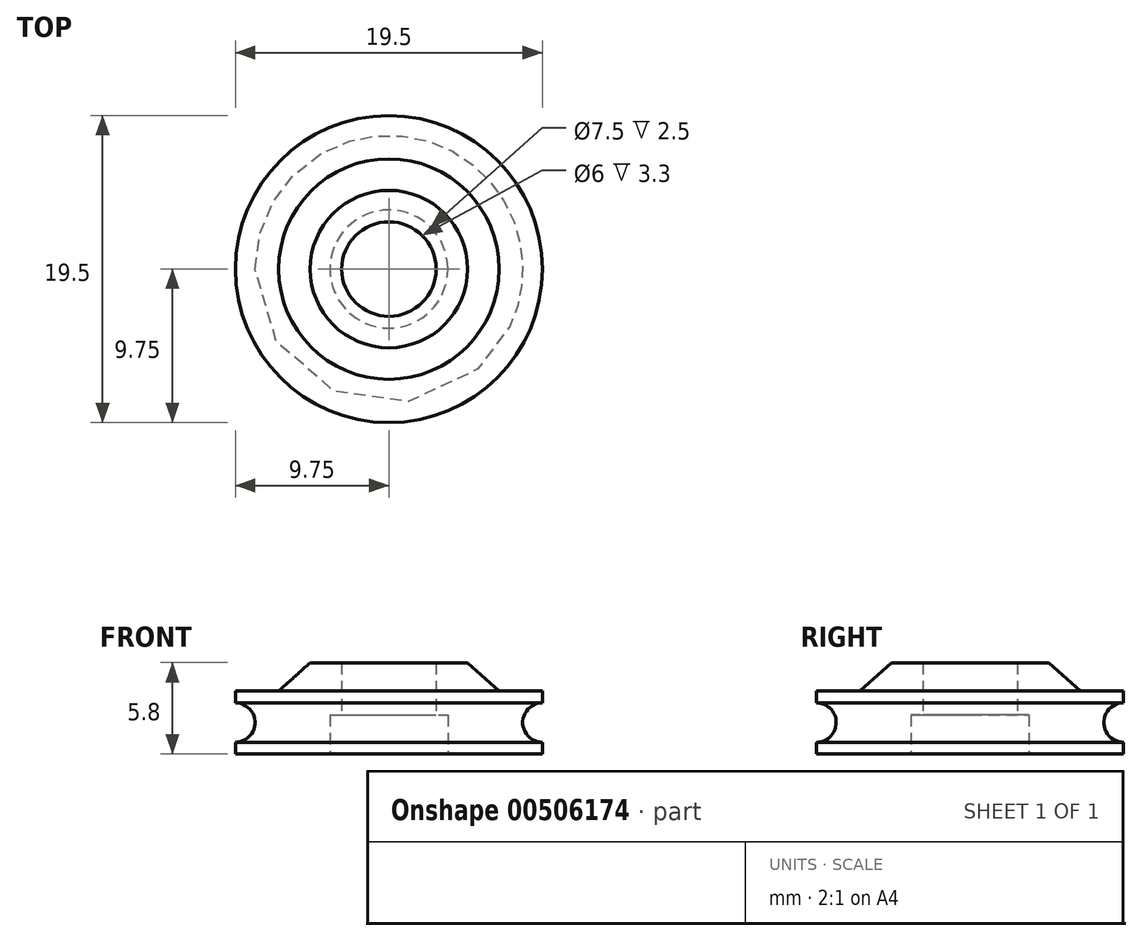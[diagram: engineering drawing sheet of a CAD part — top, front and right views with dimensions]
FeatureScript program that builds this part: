
annotation { "Feature Type Name" : "Feature", "Feature Type Description" : "" }
export const myFeature = defineFeature(function(context is Context, id is Id, definition is map)
    precondition{}
    {
        {
            var Q0;
            Q0=qCreatedBy(makeId("Front.planeOp"),FACE);
            var sketch = newSketch(context, id + "F0", { "sketchPlane" : qUnion([Q0])});
            skLineSegment(sketch, "E0", {"start": v(0, 27.32) * mm, "end": v(-9.75, 27.32) * mm});
            skLineSegment(sketch, "E1", {"start": v(-9.75, 27.32) * mm, "end": v(-9.75, 40.24) * mm});
            skPoint(sketch, "E2", {"position": v(-9.75, 29.32) * mm});
            skArc(sketch, "E3", {"start": v(-9.75, 28.07) * mm, "mid": v(-8.5, 29.32) * mm, "end": v(-9.75, 30.57) * mm});
            skLineSegment(sketch, "E4", {"start": v(0, 27.32) * mm, "end": v(0, 33.12) * mm});
            skLineSegment(sketch, "E5", {"start": v(0, 33.12) * mm, "end": v(-5, 33.12) * mm});
            skLineSegment(sketch, "E6", {"start": v(-9.75, 31.32) * mm, "end": v(-7, 31.32) * mm});
            skLineSegment(sketch, "E7", {"start": v(-7, 31.32) * mm, "end": v(-5, 33.12) * mm});
            skLineSegment(sketch, "E8", {"start": v(-3.75, 27.32) * mm, "end": v(-3.75, 29.82) * mm});
            skLineSegment(sketch, "E9", {"start": v(-3.75, 29.82) * mm, "end": v(-3, 29.82) * mm});
            skLineSegment(sketch, "E10", {"start": v(-3, 29.82) * mm, "end": v(-3, 33.12) * mm});
            skSolve(sketch);
        }
        {
            var Q0;
            {var subQ0=sQuery(id+"F0.wireOp",EDGE,"E3");Q0=makeQuery(id+"F0.imprint","IMPRINT",FACE,{"disambiguationData":[TD([[makeQuery(id+"F0.imprint","IMPRINT",EDGE,{"derivedFrom":subQ0}),-1.0]])]});}
            var Q1;
            Q1=sQuery(id+"F0.wireOp",EDGE,"E4");
            revolve(context, id + "F1", {"entities" : qUnion([Q0]), "axis" : qUnion([Q1]), "revolveType" : RevolveType.FULL});
        }
    });
